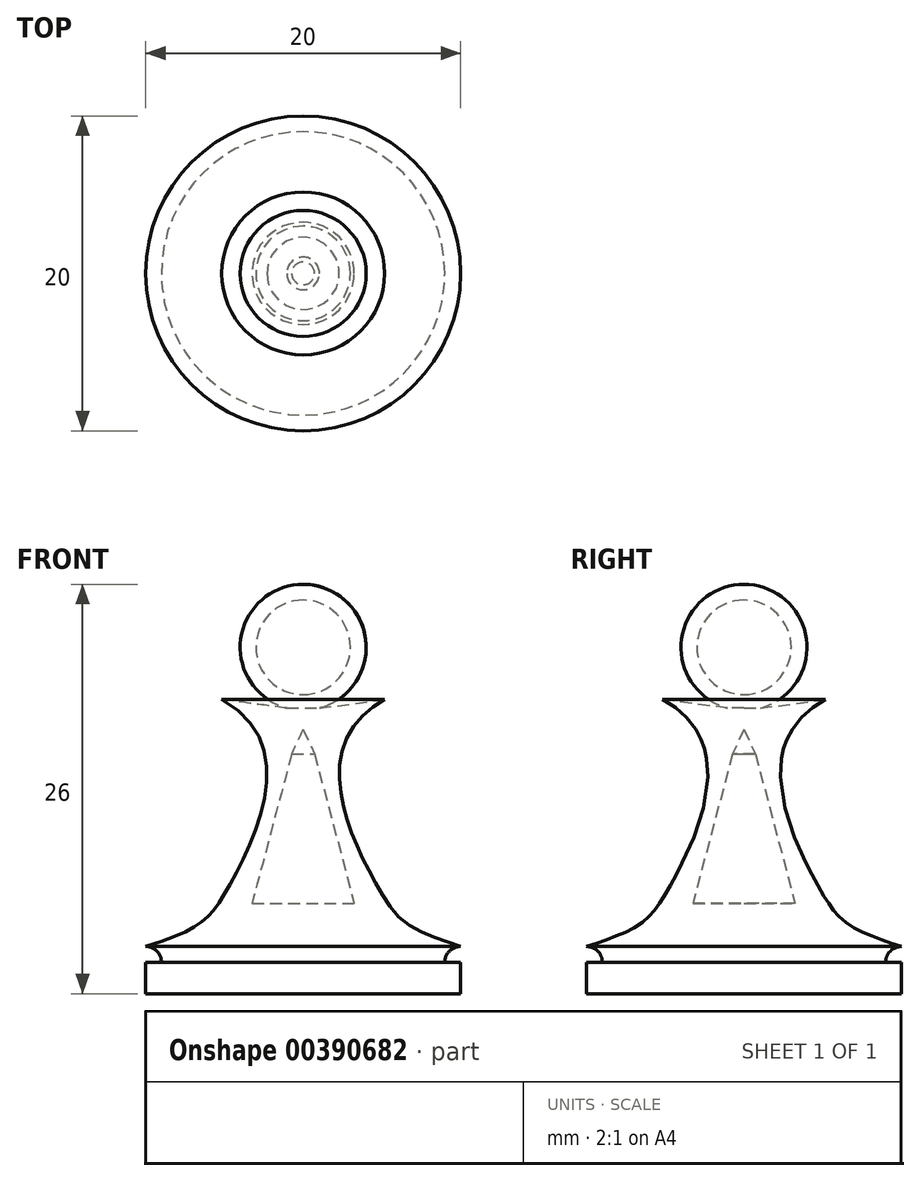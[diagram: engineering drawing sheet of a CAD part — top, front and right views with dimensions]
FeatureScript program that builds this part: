
annotation { "Feature Type Name" : "Feature", "Feature Type Description" : "" }
export const myFeature = defineFeature(function(context is Context, id is Id, definition is map)
    precondition{}
    {
        {
            var Q0;
            Q0=qCreatedBy(makeId("Front.planeOp"),FACE);
            var sketch = newSketch(context, id + "F0", { "sketchPlane" : qUnion([Q0])});
            skLineSegment(sketch, "E0", {"start": v(0, 0) * mm, "end": v(10, 0) * mm});
            skLineSegment(sketch, "E1", {"start": v(10, 0) * mm, "end": v(10, 2) * mm});
            skLineSegment(sketch, "E2", {"start": v(10, 2) * mm, "end": v(9, 2) * mm});
            skPoint(sketch, "E3.endSnap0", {"position": v(10, 1) * mm});
            skArc(sketch, "E4", {"start": v(9, 2) * mm, "mid": v(9.3, 2.7) * mm, "end": v(10, 3) * mm});
            skFitSpline(sketch, "E5", {"points": [v(10, 3) * mm, v(4.74, 6.8) * mm, v(5.18, 18.68) * mm], "startDerivative": vector(-25.14, 8.14) * mm, "endDerivative": vector(27, 14.59) * mm});
            skLineSegment(sketch, "E6", {"start": v(5.18, 18.68) * mm, "end": v(0, 18) * mm});
            skLineSegment(sketch, "E7", {"start": v(0, 0) * mm, "end": v(0, 22) * mm});
            skArc(sketch, "E8", {"start": v(0, 18) * mm, "mid": v(4, 22) * mm, "end": v(0, 26) * mm});
            skLineSegment(sketch, "E9", {"start": v(0, 22) * mm, "end": v(0, 26) * mm});
            skArc(sketch, "E10", {"start": v(0, 19) * mm, "mid": v(3, 22) * mm, "end": v(0, 25) * mm});
            skLineSegment(sketch, "E11", {"start": v(0, 5.75) * mm, "end": v(3.25, 5.75) * mm});
            skLineSegment(sketch, "E12", {"start": v(3.25, 5.75) * mm, "end": v(0.73, 15.23) * mm});
            skLineSegment(sketch, "E13", {"start": v(0.73, 15.23) * mm, "end": v(0, 16.79) * mm});
            skSolve(sketch);
        }
        {
            var Q0;
            {var subQ0=sQuery(id+"F0.wireOp",EDGE,"E8");var subQ1=sQuery(id+"F0.wireOp",EDGE,"E6");var subQ3=makeQuery(id+"F0.imprint","INTERSECT",VERTEX,{"derivedFrom":[subQ1,subQ0]});Q0=makeQuery(id+"F0.imprint","IMPRINT",FACE,{"disambiguationData":[TD([[makeQuery(id+"F0.imprint","IMPRINT",EDGE,{"disambiguationData":[TD([[subQ3,-1.0]])],"derivedFrom":subQ1}),1.0]])]});}
            var Q1;
            {var subQ0=sQuery(id+"F0.wireOp",EDGE,"E0");Q1=makeQuery(id+"F0.imprint","IMPRINT",FACE,{"disambiguationData":[TD([[makeQuery(id+"F0.imprint","IMPRINT",EDGE,{"derivedFrom":subQ0}),1.0]])]});}
            var Q2;
            {var subQ3=sQuery(id+"F0.wireOp",EDGE,"E10");Q2=makeQuery(id+"F0.imprint","IMPRINT",FACE,{"disambiguationData":[TD([[makeQuery(id+"F0.imprint","IMPRINT",EDGE,{"derivedFrom":subQ3}),-1.0]])]});}
            var Q3;
            Q3=sQuery(id+"F0.wireOp",EDGE,"E7");
            revolve(context, id + "F1", {"entities" : qUnion([Q0, Q1, Q2]), "axis" : qUnion([Q3]), "revolveType" : RevolveType.FULL});
        }
    });
